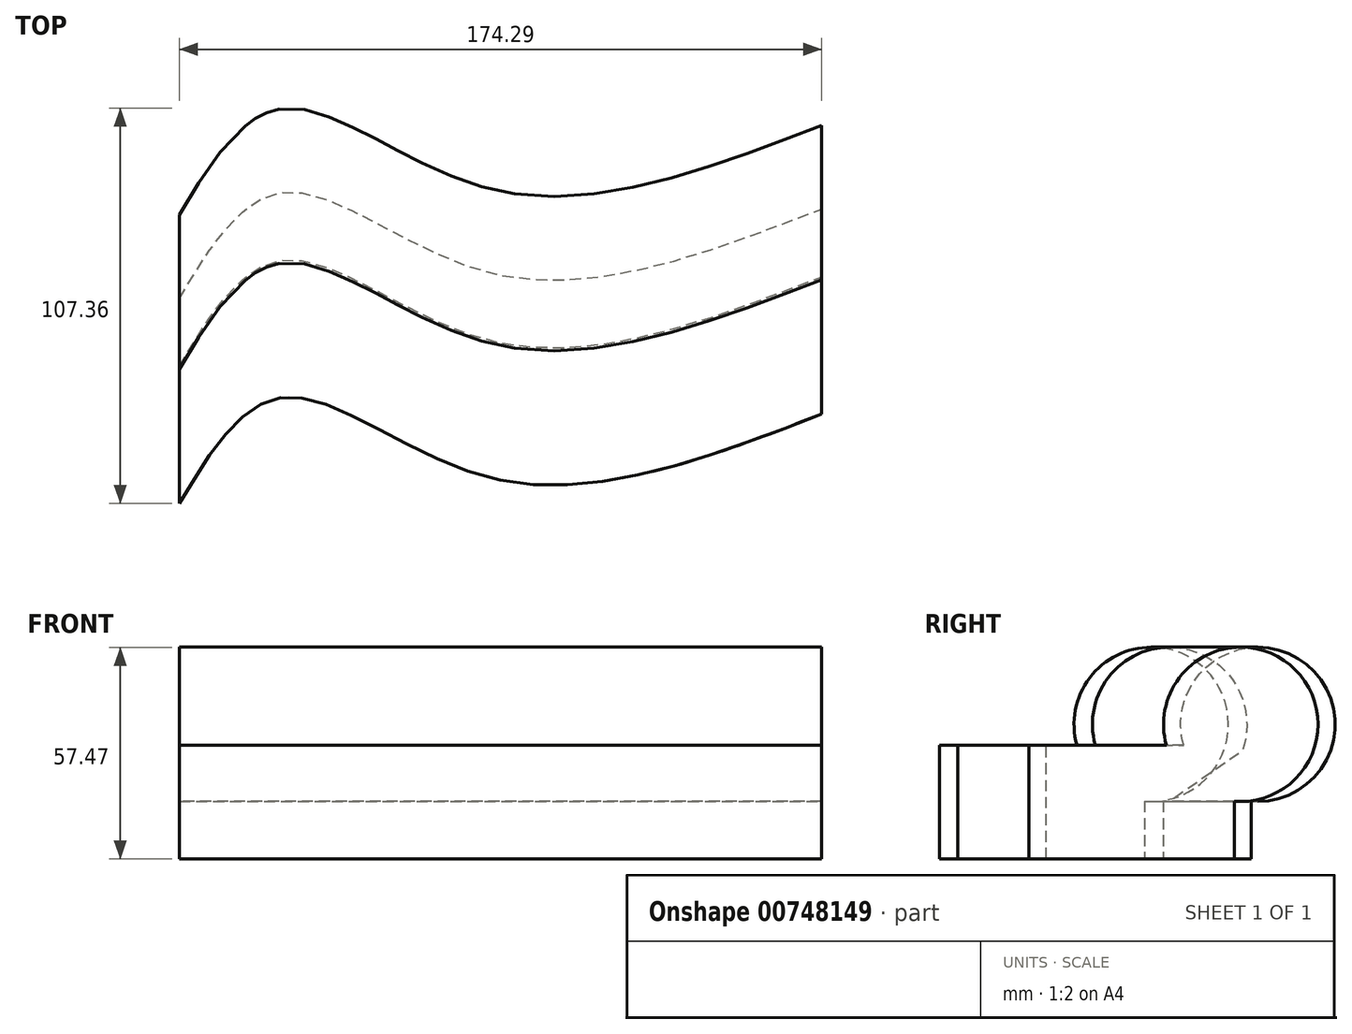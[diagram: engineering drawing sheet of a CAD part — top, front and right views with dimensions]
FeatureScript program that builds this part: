
annotation { "Feature Type Name" : "Feature", "Feature Type Description" : "" }
export const myFeature = defineFeature(function(context is Context, id is Id, definition is map)
    precondition{}
    {
        {
            var Q0;
            Q0=qCreatedBy(makeId("Right.planeOp"),FACE);
            var sketch = newSketch(context, id + "F0", { "sketchPlane" : qUnion([Q0])});
            skArc(sketch, "E0", {"start": v(26.07, 7.32) * mm, "mid": v(41.19, 44.34) * mm, "end": v(7.67, 22.52) * mm});
            skLineSegment(sketch, "E1.bottom", {"start": v(7.67, 22.52) * mm, "end": v(-29.6, 22.52) * mm});
            skLineSegment(sketch, "E1.top", {"start": v(26.07, -8.33) * mm, "end": v(-29.6, -8.33) * mm});
            skLineSegment(sketch, "E1.left", {"start": v(26.07, 7.32) * mm, "end": v(26.07, -8.33) * mm});
            skLineSegment(sketch, "E1.right", {"start": v(-29.6, 22.52) * mm, "end": v(-29.6, -8.33) * mm});
            skSolve(sketch);
        }
        {
            var Q0;
            Q0=qCreatedBy(makeId("Top.planeOp"),FACE);
            var sketch = newSketch(context, id + "F1", { "sketchPlane" : qUnion([Q0])});
            skFitSpline(sketch, "E2", {"points": [v(0, 0) * mm, v(28.55, 28.9) * mm, v(84.58, 6.91) * mm, v(174.3, 24.3) * mm], "startDerivative": vector(93.25, 155.3) * mm, "endDerivative": vector(232.17, 89.56) * mm});
            skSolve(sketch);
        }
        {
            var Q0;
            Q0=makeQuery(id+"F0.imprint","IMPRINT",FACE,{"disambiguationData":[TD([[makeQuery(id+"F0.imprint","IMPRINT",EDGE,{"derivedFrom":sQuery(id+"F0.wireOp",EDGE,"E0")}),1.0]])]});
            var Q1;
            Q1=sQuery(id+"F1.wireOp",EDGE,"E2");
            sweep(context, id + "F2", {"profiles" : qUnion([Q0]), "path" : qUnion([Q1]), "keepProfileOrientation" : true});
        }
    });
